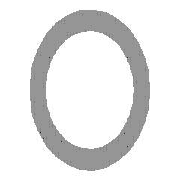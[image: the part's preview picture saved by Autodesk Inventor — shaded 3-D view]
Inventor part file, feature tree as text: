
AUTODESK INVENTOR PART (.ipt)
format: ipt  version: 2021 (Build 250183000, 183)  size: 219,648 bytes
history: native  units: mm (DEFAULTED — no unit token found)
features: other x5, plane x2, sketch x2, sweep x1
ambient origin geometry x8: Origin, YZ Plane, XZ Plane, XY Plane, X Axis, Y Axis, Z Axis, Center Point
bodies: Solid1 (feature_tree)
feature tree (10):
  parser-record x1  (decoder bookkeeping rows leaked as tree rows — omitted from the tree; the rows remain in map.json)
  other  "Driven Length"
  other  "Plano inicial"
  other  "Plano final"
  other  "Trayectoria de barrido"
  plane  "Plano de trabajo de orientación"
  sweep  "Cuerpo"
  sketch  "Sketch3"  dims[d0=26.67mm d1=2.8702mm]
  plane  "Work Plane3"
  sketch  "Sketch4"  dims[d4=-0.0mm d5=763.831936mm d6=90.0deg d7=763.831936mm d8=0.0mm d9=0.0mm]
